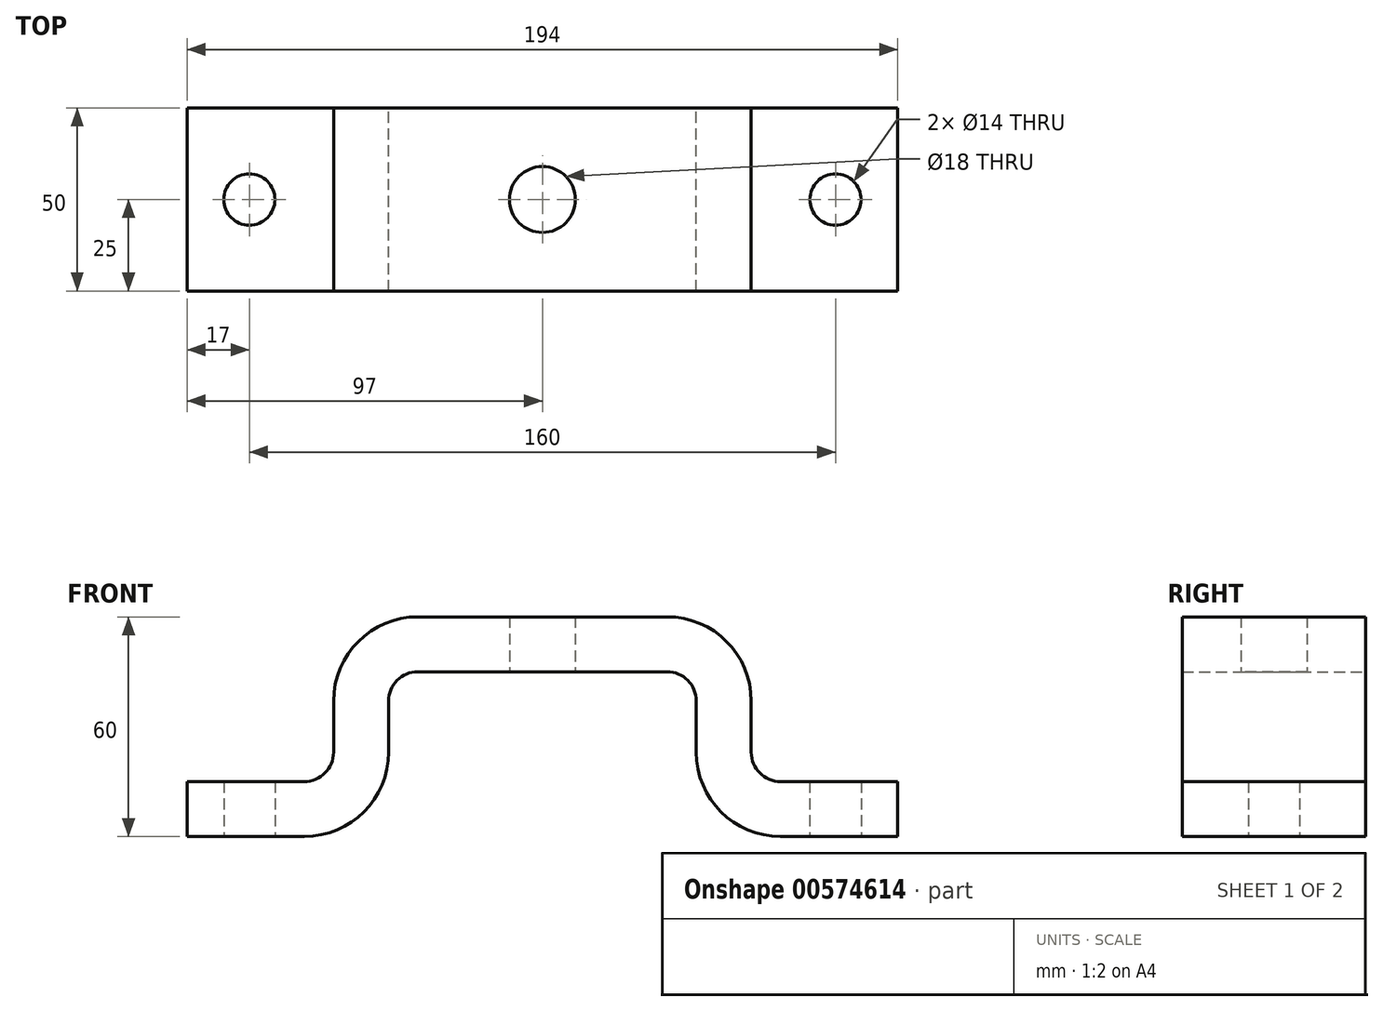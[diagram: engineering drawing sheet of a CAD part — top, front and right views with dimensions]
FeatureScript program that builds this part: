
annotation { "Feature Type Name" : "Feature", "Feature Type Description" : "" }
export const myFeature = defineFeature(function(context is Context, id is Id, definition is map)
    precondition{}
    {
        {
            var Q0;
            Q0=qCreatedBy(makeId("Front.planeOp"),FACE);
            var sketch = newSketch(context, id + "F0", { "sketchPlane" : qUnion([Q0])});
            skLineSegment(sketch, "E0", {"start": v(0, 0) * mm, "end": v(0, 15) * mm});
            skLineSegment(sketch, "E1", {"start": v(0, 15) * mm, "end": v(32, 15) * mm});
            skLineSegment(sketch, "E2", {"start": v(40, 23) * mm, "end": v(40, 37) * mm});
            skLineSegment(sketch, "E3", {"start": v(63, 60) * mm, "end": v(135, 60) * mm});
            skLineSegment(sketch, "E4", {"start": v(135, 45) * mm, "end": v(63, 45) * mm});
            skLineSegment(sketch, "E5", {"start": v(55, 37) * mm, "end": v(55, 23) * mm});
            skLineSegment(sketch, "E6", {"start": v(32, 0) * mm, "end": v(0, 0) * mm});
            skPoint(sketch, "E7.visualSharp", {"position": v(55, 45) * mm});
            skArc(sketch, "E7.filletArc", {"start": v(63, 45) * mm, "mid": v(57.34, 42.66) * mm, "end": v(55, 37) * mm});
            skPoint(sketch, "E8.visualSharp", {"position": v(40, 15) * mm});
            skArc(sketch, "E8.filletArc", {"start": v(32, 15) * mm, "mid": v(37.66, 17.34) * mm, "end": v(40, 23) * mm});
            skPoint(sketch, "E9.visualSharp", {"position": v(55, 0) * mm});
            skArc(sketch, "E9.filletArc", {"start": v(32, 0) * mm, "mid": v(48.26, 6.74) * mm, "end": v(55, 23) * mm});
            skPoint(sketch, "E10.visualSharp", {"position": v(40, 60) * mm});
            skArc(sketch, "E10.filletArc", {"start": v(63, 60) * mm, "mid": v(46.74, 53.26) * mm, "end": v(40, 37) * mm});
            skLineSegment(sketch, "E11.MirrorCS", {"start": v(194, 0) * mm, "end": v(194, 15) * mm});
            skPoint(sketch, "E12.MirrorP", {"position": v(230, 60) * mm});
            skLineSegment(sketch, "E13.MirrorCS", {"start": v(194, 15) * mm, "end": v(162, 15) * mm});
            skPoint(sketch, "E14.MirrorP", {"position": v(215, 45) * mm});
            skPoint(sketch, "E15.MirrorP", {"position": v(230, 15) * mm});
            skPoint(sketch, "E16.MirrorP", {"position": v(215, 0) * mm});
            skArc(sketch, "E17.MirrorCS", {"start": v(131, 60) * mm, "mid": v(147.26, 53.26) * mm, "end": v(154, 37) * mm});
            skArc(sketch, "E18.MirrorCS", {"start": v(162, 0) * mm, "mid": v(145.74, 6.74) * mm, "end": v(139, 23) * mm});
            skLineSegment(sketch, "E19.MirrorCS", {"start": v(154, 23) * mm, "end": v(154, 37) * mm});
            skLineSegment(sketch, "E20.MirrorCS", {"start": v(139, 37) * mm, "end": v(139, 23) * mm});
            skLineSegment(sketch, "E21.MirrorCS", {"start": v(162, 0) * mm, "end": v(194, 0) * mm});
            skLineSegment(sketch, "E22.MirrorCS", {"start": v(131, 60) * mm, "end": v(59, 60) * mm});
            skArc(sketch, "E23.MirrorCS", {"start": v(162, 15) * mm, "mid": v(156.34, 17.34) * mm, "end": v(154, 23) * mm});
            skArc(sketch, "E24.MirrorCS", {"start": v(131, 45) * mm, "mid": v(136.66, 42.66) * mm, "end": v(139, 37) * mm});
            skLineSegment(sketch, "E25.MirrorCS", {"start": v(59, 45) * mm, "end": v(131, 45) * mm});
            skSolve(sketch);
        }
        {
            var Q0;
            Q0=makeQuery(id+"F0.imprint","IMPRINT",FACE,{"disambiguationData":[TD([[makeQuery(id+"F0.imprint","IMPRINT",EDGE,{"derivedFrom":sQuery(id+"F0.wireOp",EDGE,"E0")}),-1.0]])]});
            extrude(context, id + "F1", {"entities" : qUnion([Q0]), "depth" : 50 * mm, "offsetDistance" : 25 * mm});
        }
        {
            var Q0;
            Q0=qCreatedBy(makeId("Top.planeOp"),FACE);
            var sketch = newSketch(context, id + "F2", { "sketchPlane" : qUnion([Q0])});
            skPoint(sketch, "E26", {"position": v(17, -25) * mm});
            skPoint(sketch, "E27", {"position": v(177, -25) * mm});
            skSolve(sketch);
        }
        {
            var Q0;
            Q0=makeQuery(id+"F1.opExtrude","SWEPT_FACE",FACE,{"disambiguationData":[OSD([sQuery(id+"F0.wireOp",EDGE,"E4"),sQuery(id+"F0.wireOp",EDGE,"E25.MirrorCS")])]});
            cPlane(context, id + "F3", {"entities" : qUnion([Q0]), "cplaneType" : CPlaneType.OFFSET, "offset" : 0 * mm, "width" : 150 * mm, "height" : 150 * mm});
        }
        {
            var Q0;
            Q0=qCreatedBy(id+"F3.planeOp",FACE);
            var sketch = newSketch(context, id + "F4", { "sketchPlane" : qUnion([Q0])});
            skPoint(sketch, "E28", {"position": v(97, 25) * mm});
            skSolve(sketch);
        }
        {
            var Q0;
            Q0=sQuery(id+"F4.wireOp",VERTEX,"E28");
            var Q1;
            Q1=makeQuery(id+"F1.opExtrude","SWEPT_BODY",BODY,{"disambiguationData":[OSD([sQuery(id+"F0.wireOp",EDGE,"E0"),sQuery(id+"F0.wireOp",EDGE,"E1"),sQuery(id+"F0.wireOp",EDGE,"E2"),sQuery(id+"F0.wireOp",EDGE,"E3"),sQuery(id+"F0.wireOp",EDGE,"E4"),sQuery(id+"F0.wireOp",EDGE,"E5"),sQuery(id+"F0.wireOp",EDGE,"E6"),sQuery(id+"F0.wireOp",EDGE,"E7.filletArc"),sQuery(id+"F0.wireOp",EDGE,"E8.filletArc"),sQuery(id+"F0.wireOp",EDGE,"E9.filletArc"),sQuery(id+"F0.wireOp",EDGE,"E10.filletArc"),sQuery(id+"F0.wireOp",EDGE,"E11.MirrorCS"),sQuery(id+"F0.wireOp",EDGE,"E13.MirrorCS"),sQuery(id+"F0.wireOp",EDGE,"E17.MirrorCS"),sQuery(id+"F0.wireOp",EDGE,"E18.MirrorCS"),sQuery(id+"F0.wireOp",EDGE,"E19.MirrorCS"),sQuery(id+"F0.wireOp",EDGE,"E20.MirrorCS"),sQuery(id+"F0.wireOp",EDGE,"E21.MirrorCS"),sQuery(id+"F0.wireOp",EDGE,"E22.MirrorCS"),sQuery(id+"F0.wireOp",EDGE,"E23.MirrorCS"),sQuery(id+"F0.wireOp",EDGE,"E24.MirrorCS"),sQuery(id+"F0.wireOp",EDGE,"E25.MirrorCS")])]});
            hole(context, id + "F5", {"style" : HoleStyle.SIMPLE, "endStyle" : HoleEndStyle.THROUGH, "holeDiameter" : 18 * mm, "isTappedThrough" : true, "tappedDepth" : 12 * mm, "tapClearance" : 3, "locations" : qUnion([Q0]), "scope" : qUnion([Q1])});
        }
        {
            var Q0;
            Q0=sQuery(id+"F2.wireOp",VERTEX,"E26");
            var Q1;
            Q1=makeQuery(id+"F1.opExtrude","SWEPT_BODY",BODY,{"disambiguationData":[OSD([sQuery(id+"F0.wireOp",EDGE,"E0"),sQuery(id+"F0.wireOp",EDGE,"E1"),sQuery(id+"F0.wireOp",EDGE,"E2"),sQuery(id+"F0.wireOp",EDGE,"E5"),sQuery(id+"F0.wireOp",EDGE,"E6"),sQuery(id+"F0.wireOp",EDGE,"E7.filletArc"),sQuery(id+"F0.wireOp",EDGE,"E8.filletArc"),sQuery(id+"F0.wireOp",EDGE,"E9.filletArc"),sQuery(id+"F0.wireOp",EDGE,"E10.filletArc"),sQuery(id+"F0.wireOp",EDGE,"E11.MirrorCS"),sQuery(id+"F0.wireOp",EDGE,"E13.MirrorCS"),sQuery(id+"F0.wireOp",EDGE,"E17.MirrorCS"),sQuery(id+"F0.wireOp",EDGE,"E18.MirrorCS"),sQuery(id+"F0.wireOp",EDGE,"E19.MirrorCS"),sQuery(id+"F0.wireOp",EDGE,"E20.MirrorCS"),sQuery(id+"F0.wireOp",EDGE,"E21.MirrorCS"),sQuery(id+"F0.wireOp",EDGE,"E22.MirrorCS"),sQuery(id+"F0.wireOp",EDGE,"E23.MirrorCS"),sQuery(id+"F0.wireOp",EDGE,"E24.MirrorCS"),sQuery(id+"F0.wireOp",EDGE,"E25.MirrorCS")])]});
            hole(context, id + "F6", {"style" : HoleStyle.SIMPLE, "endStyle" : HoleEndStyle.THROUGH, "oppositeDirection" : true, "holeDiameter" : 14 * mm, "isTappedThrough" : true, "tappedDepth" : 12 * mm, "tapClearance" : 3, "locations" : qUnion([Q0]), "scope" : qUnion([Q1])});
        }
        {
            var Q0;
            Q0=sQuery(id+"F2.wireOp",VERTEX,"E27");
            var Q1;
            Q1=makeQuery(id+"F1.opExtrude","SWEPT_BODY",BODY,{"disambiguationData":[OSD([sQuery(id+"F0.wireOp",EDGE,"E0"),sQuery(id+"F0.wireOp",EDGE,"E1"),sQuery(id+"F0.wireOp",EDGE,"E2"),sQuery(id+"F0.wireOp",EDGE,"E5"),sQuery(id+"F0.wireOp",EDGE,"E6"),sQuery(id+"F0.wireOp",EDGE,"E7.filletArc"),sQuery(id+"F0.wireOp",EDGE,"E8.filletArc"),sQuery(id+"F0.wireOp",EDGE,"E9.filletArc"),sQuery(id+"F0.wireOp",EDGE,"E10.filletArc"),sQuery(id+"F0.wireOp",EDGE,"E11.MirrorCS"),sQuery(id+"F0.wireOp",EDGE,"E13.MirrorCS"),sQuery(id+"F0.wireOp",EDGE,"E17.MirrorCS"),sQuery(id+"F0.wireOp",EDGE,"E18.MirrorCS"),sQuery(id+"F0.wireOp",EDGE,"E19.MirrorCS"),sQuery(id+"F0.wireOp",EDGE,"E20.MirrorCS"),sQuery(id+"F0.wireOp",EDGE,"E21.MirrorCS"),sQuery(id+"F0.wireOp",EDGE,"E22.MirrorCS"),sQuery(id+"F0.wireOp",EDGE,"E23.MirrorCS"),sQuery(id+"F0.wireOp",EDGE,"E24.MirrorCS"),sQuery(id+"F0.wireOp",EDGE,"E25.MirrorCS")])]});
            hole(context, id + "F7", {"style" : HoleStyle.SIMPLE, "endStyle" : HoleEndStyle.THROUGH, "oppositeDirection" : true, "holeDiameter" : 14 * mm, "isTappedThrough" : true, "tappedDepth" : 12 * mm, "tapClearance" : 3, "locations" : qUnion([Q0]), "scope" : qUnion([Q1])});
        }
    });
